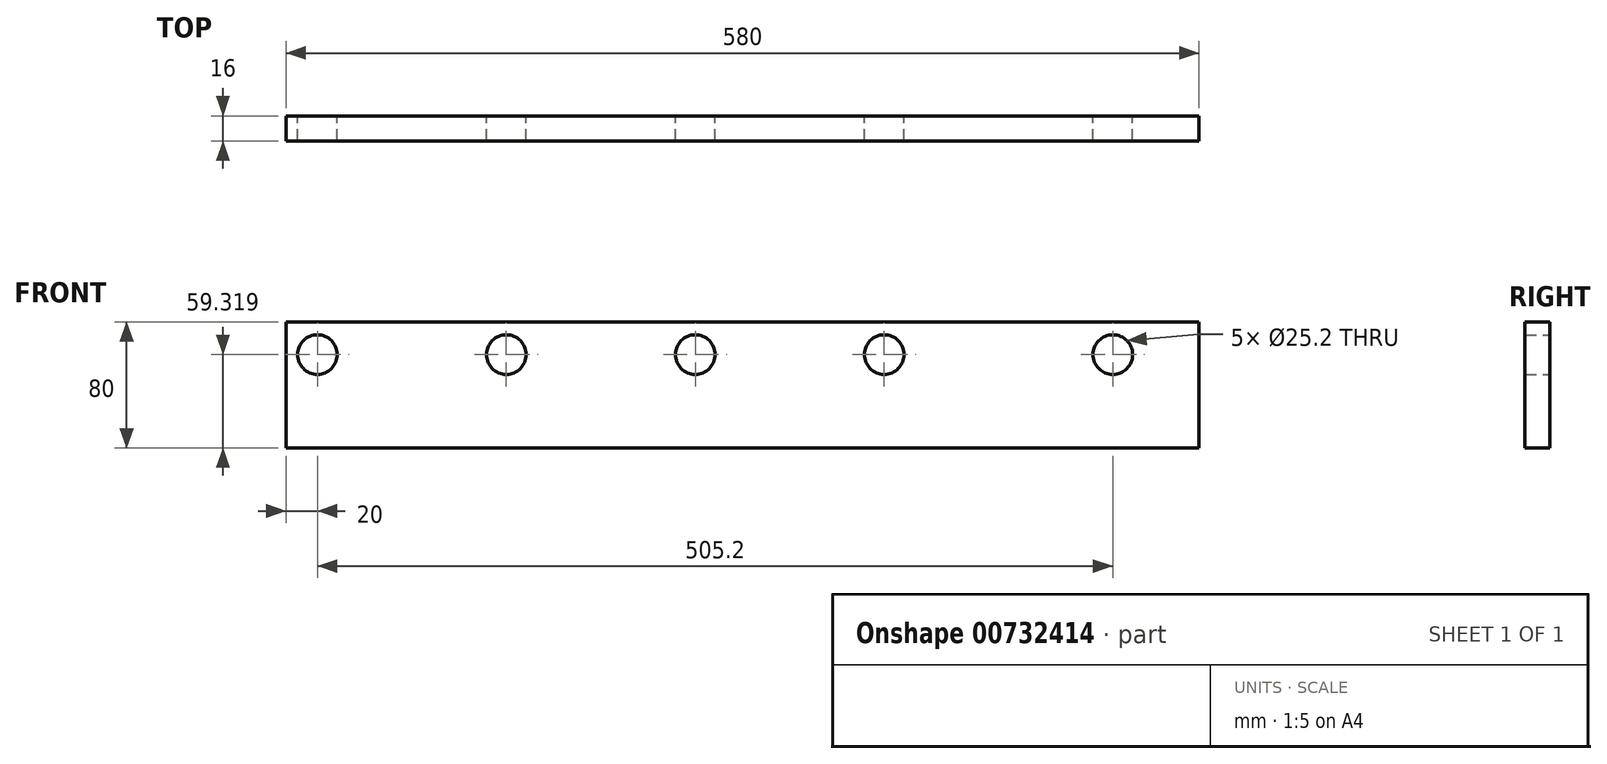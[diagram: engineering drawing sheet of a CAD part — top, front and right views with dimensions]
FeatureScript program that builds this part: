
annotation { "Feature Type Name" : "Feature", "Feature Type Description" : "" }
export const myFeature = defineFeature(function(context is Context, id is Id, definition is map)
    precondition{}
    {
        {
            var Q0;
            Q0=qCreatedBy(makeId("Front.planeOp"),FACE);
            var sketch = newSketch(context, id + "F0", { "sketchPlane" : qUnion([Q0])});
            skLineSegment(sketch, "E0.bottom", {"start": v(290, -40) * mm, "end": v(-290, -40) * mm});
            skLineSegment(sketch, "E0.top", {"start": v(290, 40) * mm, "end": v(-290, 40) * mm});
            skLineSegment(sketch, "E0.left", {"start": v(290, -40) * mm, "end": v(290, 40) * mm});
            skLineSegment(sketch, "E0.right", {"start": v(-290, -40) * mm, "end": v(-290, 40) * mm});
            skPoint(sketch, "E0.middle", {"position": v(0, 0) * mm});
            skCircle(sketch, "E1", {"center": v(-270, 19.32) * mm, "radius": 12.6 * mm});
            skCircle(sketch, "E2", {"center": v(-150, 19.32) * mm, "radius": 12.6 * mm});
            skCircle(sketch, "E3", {"center": v(-30, 19.32) * mm, "radius": 12.6 * mm});
            skCircle(sketch, "E4", {"center": v(90, 19.32) * mm, "radius": 12.6 * mm});
            skCircle(sketch, "E5", {"center": v(235.2, 19.32) * mm, "radius": 12.6 * mm});
            skSolve(sketch);
        }
        {
            var Q0;
            Q0 = qSketchRegion(id + "F0", true);
            extrude(context, id + "F1", {"entities" : qUnion([Q0]), "depth" : 16 * mm, "offsetDistance" : 25 * mm});
        }
    });
